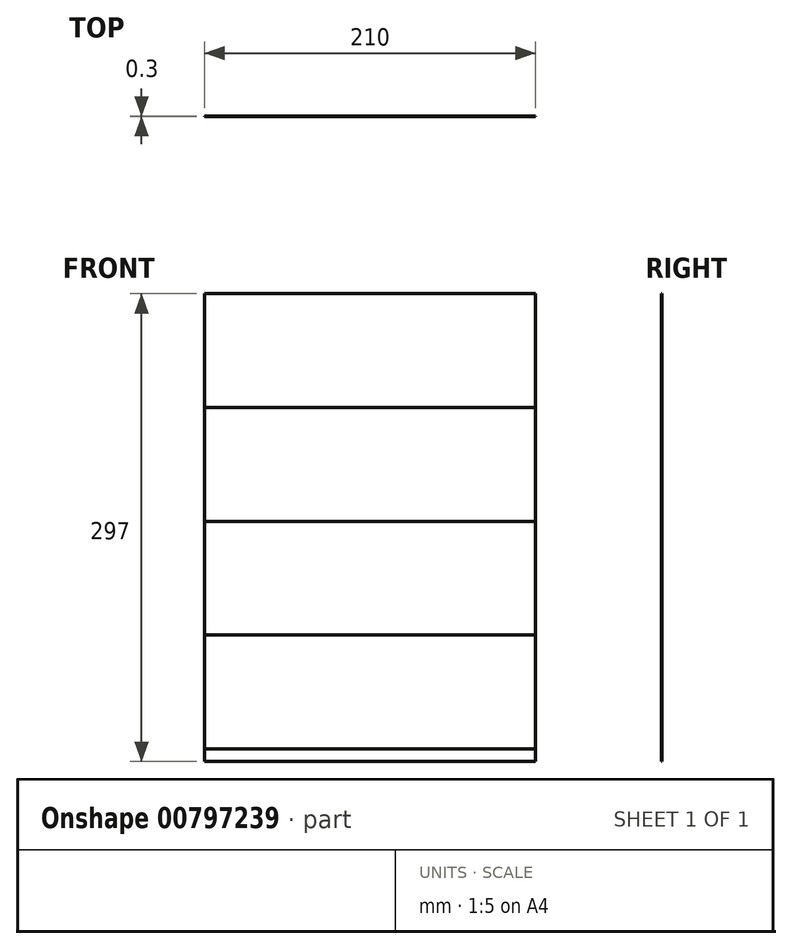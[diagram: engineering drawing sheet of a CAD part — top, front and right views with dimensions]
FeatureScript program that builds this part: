
annotation { "Feature Type Name" : "Feature", "Feature Type Description" : "" }
export const myFeature = defineFeature(function(context is Context, id is Id, definition is map)
    precondition{}
    {
        {
            var Q0;
            Q0=qCreatedBy(makeId("Front.planeOp"),FACE);
            var sketch = newSketch(context, id + "F0", { "sketchPlane" : qUnion([Q0])});
            skLineSegment(sketch, "E0.bottom", {"start": v(0, 0) * mm, "end": v(210, 0) * mm});
            skLineSegment(sketch, "E0.top", {"start": v(0, -297) * mm, "end": v(210, -297) * mm});
            skLineSegment(sketch, "E0.left", {"start": v(0, 0) * mm, "end": v(0, -297) * mm});
            skLineSegment(sketch, "E0.right", {"start": v(210, 0) * mm, "end": v(210, -297) * mm});
            skSolve(sketch);
        }
        {
            var Q0;
            Q0=makeQuery(id+"F0.imprint","IMPRINT",FACE,{"disambiguationData":[TD([[makeQuery(id+"F0.imprint","IMPRINT",EDGE,{"derivedFrom":sQuery(id+"F0.wireOp",EDGE,"E0.bottom")}),-1.0]])]});
            extrude(context, id + "F1", {"entities" : qUnion([Q0]), "depth" : 0.3 * mm, "offsetDistance" : 25 * mm});
        }
        {
            var Q0;
            Q0=makeQuery(id+"F1.opExtrude","CAP_FACE",FACE,{"disambiguationData":[OSD([sQuery(id+"F0.wireOp",EDGE,"E0.bottom"),sQuery(id+"F0.wireOp",EDGE,"E0.top"),sQuery(id+"F0.wireOp",EDGE,"E0.left"),sQuery(id+"F0.wireOp",EDGE,"E0.right")])],"isStart":true});
            var sketch = newSketch(context, id + "F2", { "sketchPlane" : qUnion([Q0])});
            skLineSegment(sketch, "E1.bottom", {"start": v(0, 0) * mm, "end": v(-210, 0) * mm});
            skLineSegment(sketch, "E1.top", {"start": v(0, -72.25) * mm, "end": v(-210, -72.25) * mm});
            skLineSegment(sketch, "E1.left", {"start": v(0, 0) * mm, "end": v(0, -72.25) * mm});
            skLineSegment(sketch, "E1.right", {"start": v(-210, 0) * mm, "end": v(-210, -72.25) * mm});
            skLineSegment(sketch, "E2.top", {"start": v(0, -144.5) * mm, "end": v(-210, -144.5) * mm});
            skLineSegment(sketch, "E2.left", {"start": v(0, -72.25) * mm, "end": v(0, -144.5) * mm});
            skLineSegment(sketch, "E2.right", {"start": v(-210, -72.25) * mm, "end": v(-210, -144.5) * mm});
            skLineSegment(sketch, "E3.top", {"start": v(0, -216.75) * mm, "end": v(-210, -216.75) * mm});
            skLineSegment(sketch, "E3.left", {"start": v(0, -144.5) * mm, "end": v(0, -216.75) * mm});
            skLineSegment(sketch, "E3.right", {"start": v(-210, -144.5) * mm, "end": v(-210, -216.75) * mm});
            skLineSegment(sketch, "E4.top", {"start": v(0, -289) * mm, "end": v(-210, -289) * mm});
            skLineSegment(sketch, "E4.left", {"start": v(0, -216.75) * mm, "end": v(0, -289) * mm});
            skLineSegment(sketch, "E4.right", {"start": v(-210, -216.75) * mm, "end": v(-210, -289) * mm});
            skSolve(sketch);
        }
        {
            var Q0;
            Q0=makeQuery(id+"F2.imprint","IMPRINT",FACE,{"disambiguationData":[TD([[makeQuery(id+"F2.imprint","IMPRINT",EDGE,{"derivedFrom":sQuery(id+"F2.wireOp",EDGE,"E1.bottom")}),1.0]])]});
            extrude(context, id + "F3", {"entities" : qUnion([Q0]), "oppositeDirection" : true, "depth" : 0.3 * mm, "offsetDistance" : 25 * mm});
        }
        {
            var Q0;
            Q0=makeQuery(id+"F2.imprint","IMPRINT",FACE,{"disambiguationData":[TD([[makeQuery(id+"F2.imprint","IMPRINT",EDGE,{"derivedFrom":sQuery(id+"F2.wireOp",EDGE,"E1.top")}),1.0]])]});
            var Q1;
            Q1=sQuery(id+"F2.wireOp",EDGE,"E2.right");
            var Q2;
            Q2=sQuery(id+"F2.wireOp",EDGE,"E1.top");
            var Q3;
            Q3=sQuery(id+"F2.wireOp",EDGE,"E2.top");
            var Q4;
            Q4=sQuery(id+"F2.wireOp",EDGE,"E2.left");
            extrude(context, id + "F4", {"entities" : qUnion([Q0]), "surfaceEntities" : qUnion([Q1, Q2, Q3, Q4]), "oppositeDirection" : true, "depth" : 0.3 * mm, "offsetDistance" : 25 * mm});
        }
        {
            var Q0;
            Q0=makeQuery(id+"F2.imprint","IMPRINT",FACE,{"disambiguationData":[TD([[makeQuery(id+"F2.imprint","IMPRINT",EDGE,{"derivedFrom":sQuery(id+"F2.wireOp",EDGE,"E2.top")}),1.0]])]});
            var Q1;
            Q1=sQuery(id+"F2.wireOp",EDGE,"E3.right");
            var Q2;
            Q2=sQuery(id+"F2.wireOp",EDGE,"E2.top");
            var Q3;
            Q3=sQuery(id+"F2.wireOp",EDGE,"E3.top");
            var Q4;
            Q4=sQuery(id+"F2.wireOp",EDGE,"E3.left");
            extrude(context, id + "F5", {"entities" : qUnion([Q0]), "surfaceEntities" : qUnion([Q1, Q2, Q3, Q4]), "oppositeDirection" : true, "depth" : 0.3 * mm, "offsetDistance" : 25 * mm});
        }
        {
            var Q0;
            Q0=makeQuery(id+"F2.imprint","IMPRINT",FACE,{"disambiguationData":[TD([[makeQuery(id+"F2.imprint","IMPRINT",EDGE,{"derivedFrom":sQuery(id+"F2.wireOp",EDGE,"E3.top")}),1.0]])]});
            var Q1;
            Q1=sQuery(id+"F2.wireOp",EDGE,"E3.top");
            var Q2;
            Q2=sQuery(id+"F2.wireOp",EDGE,"E4.right");
            var Q3;
            Q3=sQuery(id+"F2.wireOp",EDGE,"E4.top");
            var Q4;
            Q4=sQuery(id+"F2.wireOp",EDGE,"E4.left");
            extrude(context, id + "F6", {"entities" : qUnion([Q0]), "surfaceEntities" : qUnion([Q1, Q2, Q3, Q4]), "oppositeDirection" : true, "depth" : 0.3 * mm, "offsetDistance" : 25 * mm});
        }
    });
